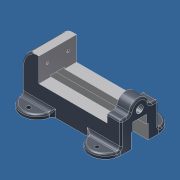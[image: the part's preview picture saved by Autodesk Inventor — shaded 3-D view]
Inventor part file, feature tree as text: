
AUTODESK INVENTOR PART (.ipt)
format: ipt  version: unknown  size: 463,360 bytes
history: native  units: in
note: dims shown in document units (in); Inventor stores cm internally (conversion verified against a paired STEP export)
features: sketch x10, extrude x7, hole x3, fillet x2, projected_geometry x1
ambient origin geometry x8: Origin, YZ Plane, XZ Plane, XY Plane, X Axis, Y Axis, Z Axis, Center Point
bodies: Solid1 (feature_tree)
feature tree (23):
  extrude  "Extrusion1"  Depth=3.312in
  extrude  "Extrusion2"  Depth=5.0in
  extrude  "Extrusion3"  Depth=2.75in TaperAngle=0.0deg
  extrude  "Extrusion4"  Depth=1.187in
  extrude  "Extrusion5"  Depth=1.0in TaperAngle=0.0deg
  extrude  "Extrusion6"  Depth=0.626in
  extrude  "Extrusion7"  Depth=1.0in TaperAngle=0.0deg
  hole  "Hole1"  [1 undecoded]
  hole  "Hole2"  [1 undecoded]
  hole  "Hole3"  [1 undecoded]
  fillet  "Fillet1"  Radius=1.125in
  fillet  "Fillet2"  Radius=1.125in
  sketch  "Sketch1"  dims[d0=7.25in d1=3.312in]
  sketch  "Sketch2"  dims[d2=1.25in d3=5.0in]
  sketch  "Sketch3"  dims[d4=2.187in d5=2.75in d6=0.0in]
  sketch  "Sketch4"  dims[d8=1.0in d9=0.0in d10=1.187in]
  sketch  "Sketch6"  dims[d11=1.375in d12=1.0in d13=0.0in]
  sketch  "Sketch7"  dims[d14=0.626in d15=0.626in]
  sketch  "Sketch8"  dims[d17=1.062in d18=1.0in d19=0.0in]
  projected_geometry  "Projected Loop1"
  sketch  "Sketch9"  dims[d21=2.25in d23=1.002in]
  sketch  "Sketch10"  dims[d25=6.0in d26=0.0in d27=0.125in]
  sketch  "Sketch11"  dims[d28=6.0in d29=0.0in d30=1.562in d31=1.125in d32=1.125in d33=1.125in d34=1.125in d35=0.312in d36=0.0in d37=0.527in d38=0.75in d39=0.375in d40=0.25in d41=0.5635in d42=1.0in d43=0.8108in d44=1.125in d45=5.0in d46=1.125in d47=4.0in d48=5.0in d49=4.0in d50=0.625in d51=0.625in d52=0.312in d53=0.75in d54=0.375in d55=0.25in d56=0.5635in d57=0.312in d58=0.0in d59=1.0in d60=1.0in d61=1.5in d62=0.625in d63=0.196in d64=0.625in d65=0.375in d66=0.25in d67=0.5635in d68=0.625in d69=0.0in d70=0.25in d71=0.125in]
note: 3 required parameter values undecoded (feature->parameter linkage not recoverable at this tier; creation-order binding heuristic only, values carry confidence <= 0.55)
